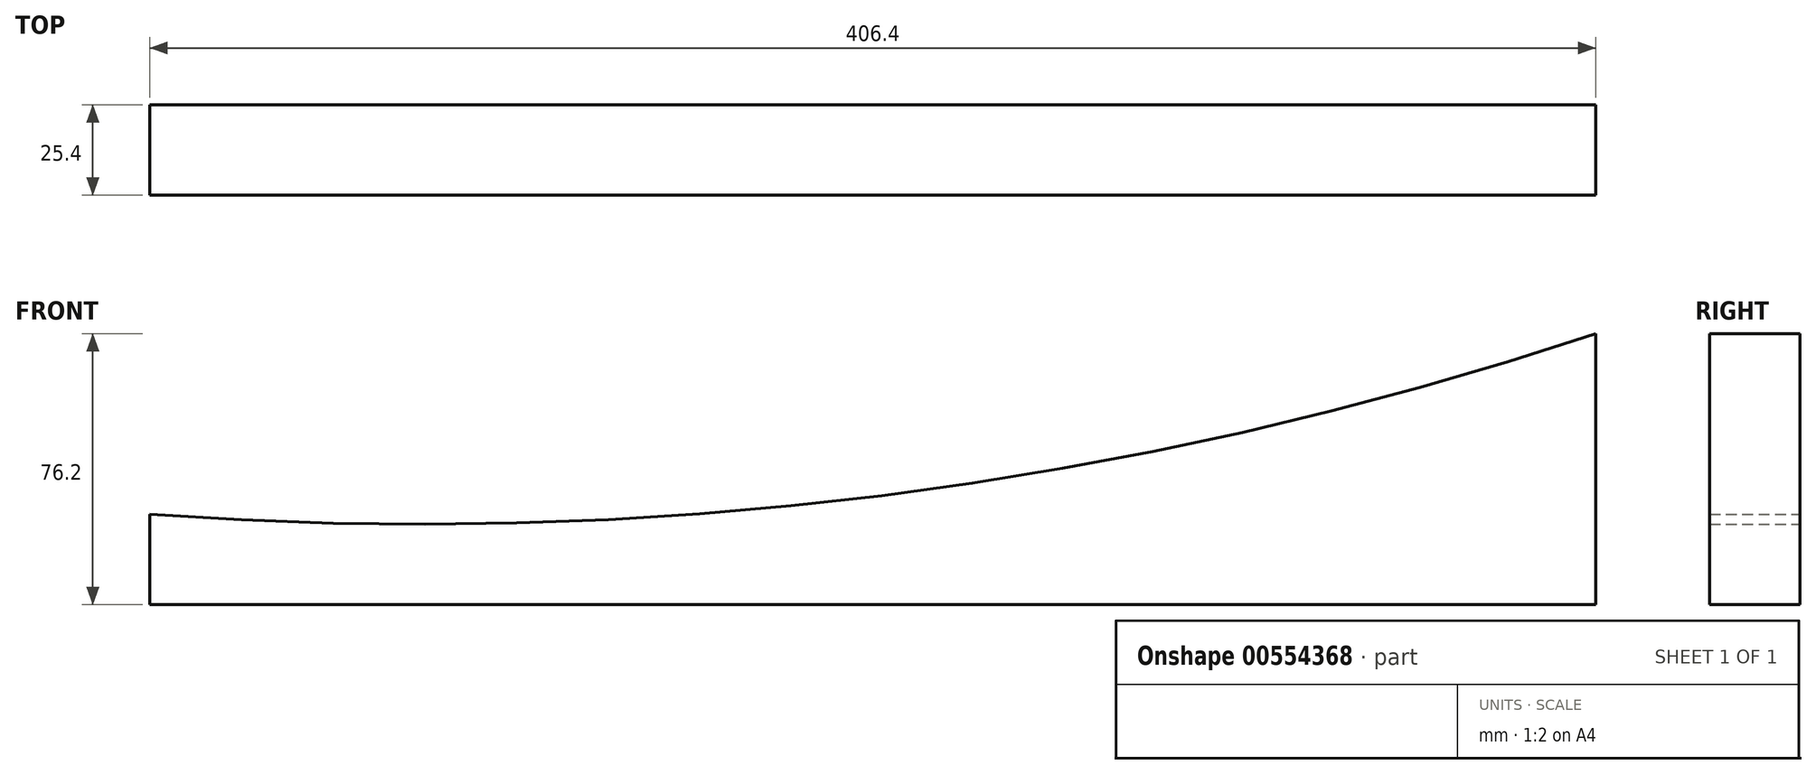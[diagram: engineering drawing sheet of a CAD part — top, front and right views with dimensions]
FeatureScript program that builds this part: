
annotation { "Feature Type Name" : "Feature", "Feature Type Description" : "" }
export const myFeature = defineFeature(function(context is Context, id is Id, definition is map)
    precondition{}
    {
        {
            var Q0;
            Q0=qCreatedBy(makeId("Front.planeOp"),FACE);
            var sketch = newSketch(context, id + "F0", { "sketchPlane" : qUnion([Q0])});
            skLineSegment(sketch, "E0", {"start": v(0, 0) * mm, "end": v(0, 25.4) * mm});
            skLineSegment(sketch, "E1", {"start": v(0, 0) * mm, "end": v(406.4, 0) * mm});
            skLineSegment(sketch, "E2", {"start": v(406.4, 0) * mm, "end": v(406.4, 76.2) * mm});
            skArc(sketch, "E3", {"start": v(0, 25.4) * mm, "mid": v(205.72, 30.66) * mm, "end": v(406.4, 76.2) * mm});
            skSolve(sketch);
        }
        {
            var Q0;
            Q0 = qSketchRegion(id + "F0", true);
            extrude(context, id + "F1", {"entities" : qUnion([Q0]), "depth" : 25.4 * mm, "offsetDistance" : 25.4 * mm});
        }
    });
